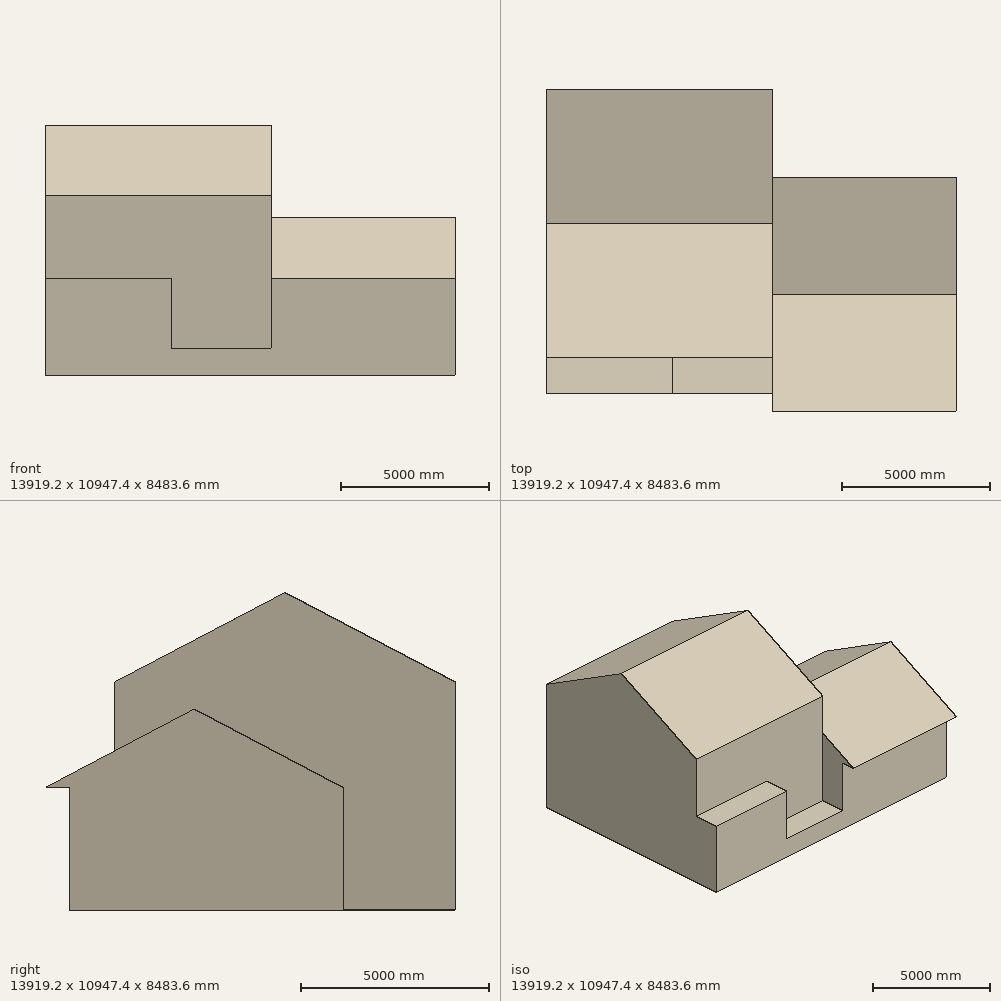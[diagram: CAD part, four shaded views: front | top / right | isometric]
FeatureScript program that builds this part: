
annotation { "Feature Type Name" : "Feature", "Feature Type Description" : "" }
export const myFeature = defineFeature(function(context is Context, id is Id, definition is map)
    precondition{}
    {
        {
            var Q0;
            Q0=qCreatedBy(makeId("Right.planeOp"),FACE);
            cPlane(context, id + "F0", {"entities" : qUnion([Q0]), "cplaneType" : CPlaneType.OFFSET, "offset" : 6248.4 * mm, "width" : 152.4 * mm, "height" : 152.4 * mm});
        }
        {
            var Q0;
            Q0=qCreatedBy(makeId("Right.planeOp"),FACE);
            cPlane(context, id + "F1", {"entities" : qUnion([Q0]), "cplaneType" : CPlaneType.OFFSET, "offset" : 7670.8 * mm, "oppositeDirection" : true, "width" : 152.4 * mm, "height" : 152.4 * mm});
        }
        {
            var Q0;
            Q0=qCreatedBy(id+"F0.planeOp",FACE);
            var sketch = newSketch(context, id + "F2", { "sketchPlane" : qUnion([Q0])});
            skLineSegment(sketch, "E0", {"start": v(0, 0) * mm, "end": v(7315.2, 0) * mm});
            skLineSegment(sketch, "E1.0", {"start": v(7315.2, 0) * mm, "end": v(7315.2, 3276.6) * mm});
            skLineSegment(sketch, "E2.MirrorCS", {"start": v(3340.1, 5372.1) * mm, "end": v(-635, 3276.6) * mm});
            skLineSegment(sketch, "E3.MirrorCS", {"start": v(0, 3276.6) * mm, "end": v(-635, 3276.6) * mm});
            skLineSegment(sketch, "E4.MirrorCS", {"start": v(3340.1, 5372.1) * mm, "end": v(7315.2, 3276.6) * mm});
            skLineSegment(sketch, "E5.0", {"start": v(0, 6.35) * mm, "end": v(7315.2, 6.35) * mm});
            skLineSegment(sketch, "E6", {"start": v(0, 6.35) * mm, "end": v(0, 3276.6) * mm});
            skSolve(sketch);
        }
        {
            var Q0;
            Q0=qCreatedBy(makeId("Right.planeOp"),FACE);
            var sketch = newSketch(context, id + "F3", { "sketchPlane" : qUnion([Q0])});
            skLineSegment(sketch, "E7", {"start": v(0, 0) * mm, "end": v(10312.4, 0) * mm});
            skLineSegment(sketch, "E8.0", {"start": v(0, 914.4) * mm, "end": v(1219.2, 914.4) * mm});
            skLineSegment(sketch, "E9.0", {"start": v(1219.2, 914.4) * mm, "end": v(1219.2, 6096) * mm});
            skLineSegment(sketch, "E10.0", {"start": v(10312.4, 0) * mm, "end": v(10312.4, 6096) * mm});
            skLineSegment(sketch, "E11", {"start": v(1219.2, 6096) * mm, "end": v(5765.8, 8483.6) * mm});
            skLineSegment(sketch, "E12", {"start": v(5765.8, 8483.6) * mm, "end": v(10312.4, 6096) * mm});
            skLineSegment(sketch, "E13", {"start": v(0, 0) * mm, "end": v(0, 914.4) * mm});
            skLineSegment(sketch, "E14.0", {"start": v(0, 6.35) * mm, "end": v(10312.4, 6.35) * mm});
            skLineSegment(sketch, "E15.0", {"start": v(0, 12.7) * mm, "end": v(10312.4, 12.7) * mm});
            skSolve(sketch);
        }
        {
            var Q0;
            Q0=qCreatedBy(id+"F1.planeOp",FACE);
            var sketch = newSketch(context, id + "F4", { "sketchPlane" : qUnion([Q0])});
            skLineSegment(sketch, "E16", {"start": v(0, 0) * mm, "end": v(10312.4, 0) * mm});
            skLineSegment(sketch, "E17", {"start": v(0, 0) * mm, "end": v(0, 3276.6) * mm});
            skLineSegment(sketch, "E18.0", {"start": v(10312.4, 0) * mm, "end": v(10312.4, 6096) * mm});
            skLineSegment(sketch, "E19.0", {"start": v(0, 3276.6) * mm, "end": v(1219.2, 3276.6) * mm});
            skLineSegment(sketch, "E20.0", {"start": v(1219.2, 3276.6) * mm, "end": v(1219.2, 6096) * mm});
            skLineSegment(sketch, "E21", {"start": v(1219.2, 6096) * mm, "end": v(5765.8, 8483.6) * mm});
            skLineSegment(sketch, "E22", {"start": v(10312.4, 6096) * mm, "end": v(5765.8, 8483.6) * mm});
            skSolve(sketch);
        }
        {
            var Q0;
            Q0=qCreatedBy(makeId("Right.planeOp"),FACE);
            cPlane(context, id + "F5", {"entities" : qUnion([Q0]), "cplaneType" : CPlaneType.OFFSET, "offset" : 6705.6 * mm, "width" : 152.4 * mm, "height" : 152.4 * mm});
        }
        {
            var Q0;
            Q0=qCreatedBy(makeId("Right.planeOp"),FACE);
            cPlane(context, id + "F6", {"entities" : qUnion([Q0]), "cplaneType" : CPlaneType.OFFSET, "offset" : 8128 * mm, "oppositeDirection" : true, "width" : 152.4 * mm, "height" : 152.4 * mm});
        }
        {
            var Q0;
            {var subQ0=sQuery(id+"F3.wireOp",EDGE,"E8.0");Q0=makeQuery(id+"F3.imprint","IMPRINT",FACE,{"disambiguationData":[TD([[makeQuery(id+"F3.imprint","IMPRINT",EDGE,{"derivedFrom":subQ0}),-1.0]])]});}
            extrude(context, id + "F7", {"entities" : qUnion([Q0]), "oppositeDirection" : true, "depth" : 3403.6 * mm});
        }
        {
            var Q0;
            Q0=makeQuery(id+"F2.imprint","IMPRINT",FACE,{"disambiguationData":[TD([[makeQuery(id+"F2.imprint","IMPRINT",EDGE,{"derivedFrom":sQuery(id+"F2.wireOp",EDGE,"E2.MirrorCS")}),1.0]])]});
            extrude(context, id + "F8", {"entities" : qUnion([Q0]), "operationType" : NewBodyOperationType.ADD, "oppositeDirection" : true, "depth" : 6248.4 * mm});
        }
        {
            var Q0;
            Q0=makeQuery(id+"F4.imprint","IMPRINT",FACE,{"disambiguationData":[TD([[makeQuery(id+"F4.imprint","IMPRINT",EDGE,{"derivedFrom":sQuery(id+"F4.wireOp",EDGE,"E16")}),1.0]])]});
            extrude(context, id + "F9", {"entities" : qUnion([Q0]), "operationType" : NewBodyOperationType.ADD, "depth" : 4267.2 * mm});
        }
    });
